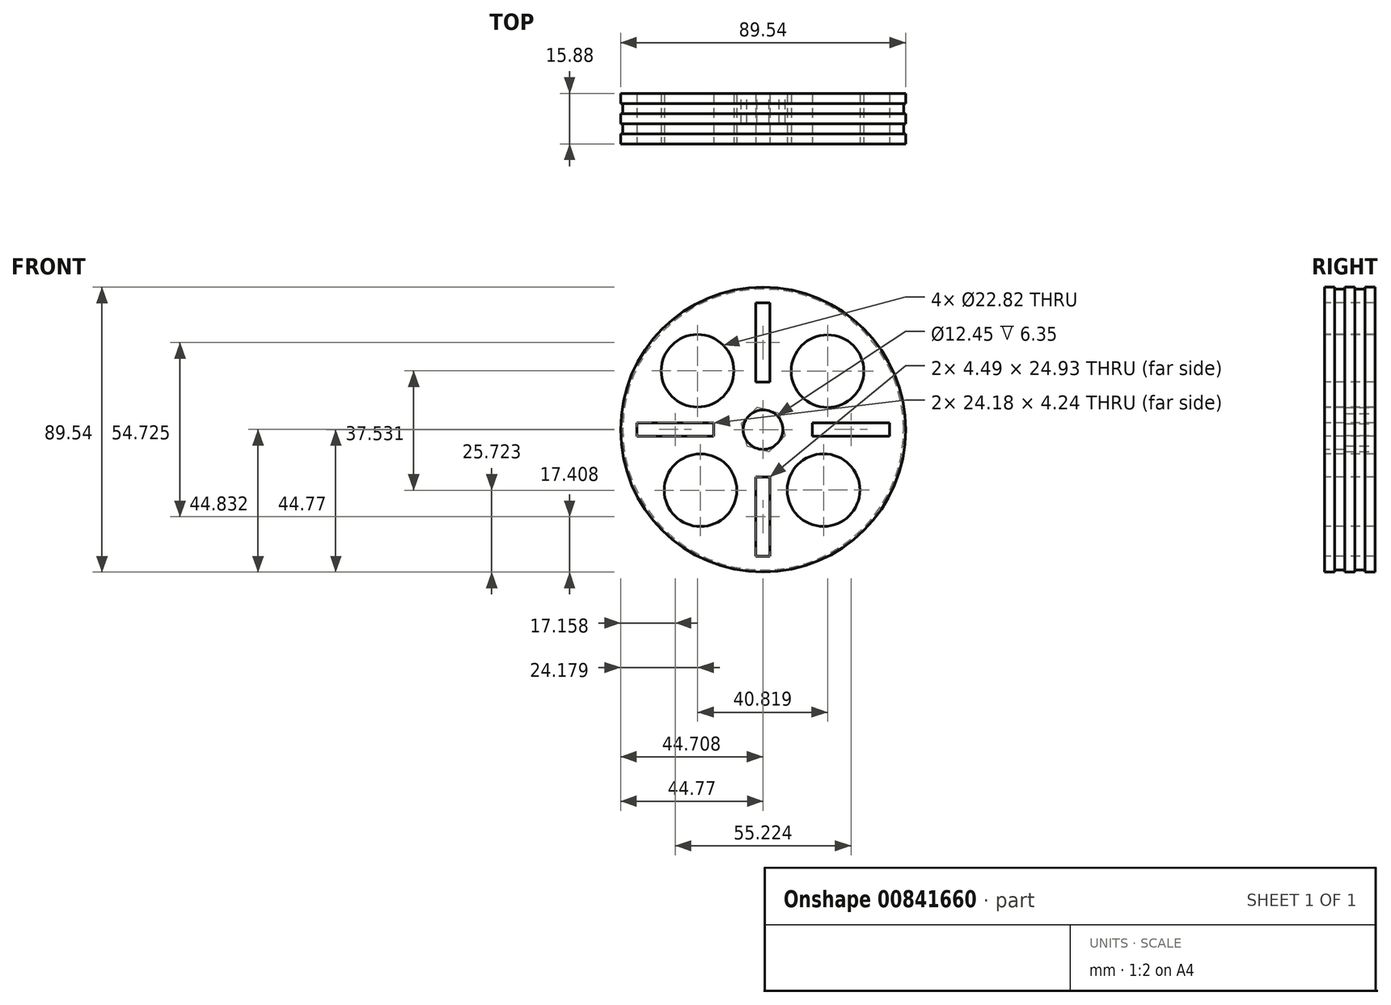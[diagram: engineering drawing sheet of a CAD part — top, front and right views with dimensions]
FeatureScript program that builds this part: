
annotation { "Feature Type Name" : "Feature", "Feature Type Description" : "" }
export const myFeature = defineFeature(function(context is Context, id is Id, definition is map)
    precondition{}
    {
        {
            var Q0;
            Q0=qCreatedBy(makeId("Front.planeOp"),FACE);
            var sketch = newSketch(context, id + "F0", { "sketchPlane" : qUnion([Q0])});
            skCircle(sketch, "E0", {"center": v(0, 0) * mm, "radius": 44.13 * mm});
            skSolve(sketch);
        }
        {
            var Q0;
            Q0 = qSketchRegion(id + "F0", true);
            extrude(context, id + "F1", {"entities" : qUnion([Q0]), "oppositeDirection" : true, "depth" : 3.17 * mm, "offsetDistance" : 25.4 * mm});
        }
        {
            var Q0;
            Q0=qCreatedBy(makeId("Front.planeOp"),FACE);
            var sketch = newSketch(context, id + "F2", { "sketchPlane" : qUnion([Q0])});
            skCircle(sketch, "E1", {"center": v(0, 0) * mm, "radius": 44.77 * mm});
            skSolve(sketch);
        }
        {
            var Q0;
            Q0 = qSketchRegion(id + "F2", true);
            var Q1;
            Q1 = qSketchRegion(id + "F0", true);
            extrude(context, id + "F3", {"entities" : qUnion([Q0, Q1]), "operationType" : NewBodyOperationType.ADD, "depth" : 3.17 * mm, "offsetDistance" : 25.4 * mm});
        }
        {
            var Q0;
            Q0=makeQuery(id+"F3.boolean.opBoolean","MERGE",FACE,{"derivedFrom":[makeQuery(id+"F3.opExtrude","CAP_FACE",FACE,{"disambiguationData":[OSD([sQuery(id+"F0.wireOp",EDGE,"E0")])],"isStart":false}),makeQuery(id+"F3.opExtrude","CAP_FACE",FACE,{"disambiguationData":[OSD([sQuery(id+"F2.wireOp",EDGE,"E1")])],"isStart":false})]});
            var sketch = newSketch(context, id + "F4", { "sketchPlane" : qUnion([Q0])});
            skCircle(sketch, "E2", {"center": v(0, 0) * mm, "radius": 44.13 * mm});
            skSolve(sketch);
        }
        {
            var Q0;
            Q0 = qSketchRegion(id + "F4", true);
            extrude(context, id + "F5", {"entities" : qUnion([Q0]), "operationType" : NewBodyOperationType.ADD, "depth" : 3.17 * mm, "offsetDistance" : 25.4 * mm});
        }
        {
            var Q0;
            Q0=makeQuery(id+"F5.opExtrude","CAP_FACE",FACE,{"disambiguationData":[OSD([sQuery(id+"F4.wireOp",EDGE,"E2")])],"isStart":false});
            var sketch = newSketch(context, id + "F6", { "sketchPlane" : qUnion([Q0])});
            skCircle(sketch, "E3", {"center": v(0, 0) * mm, "radius": 44.77 * mm});
            skSolve(sketch);
        }
        {
            var Q0;
            Q0 = qSketchRegion(id + "F6", true);
            extrude(context, id + "F7", {"entities" : qUnion([Q0]), "operationType" : NewBodyOperationType.ADD, "depth" : 3.17 * mm, "offsetDistance" : 25.4 * mm});
        }
        {
            var Q0;
            Q0=makeQuery(id+"F1.opExtrude","CAP_FACE",FACE,{"disambiguationData":[OSD([sQuery(id+"F0.wireOp",EDGE,"E0")])],"isStart":false});
            var sketch = newSketch(context, id + "F8", { "sketchPlane" : qUnion([Q0])});
            skCircle(sketch, "E4", {"center": v(0, 0) * mm, "radius": 44.77 * mm});
            skSolve(sketch);
        }
        {
            var Q0;
            Q0 = qSketchRegion(id + "F8", true);
            extrude(context, id + "F9", {"entities" : qUnion([Q0]), "operationType" : NewBodyOperationType.ADD, "depth" : 3.17 * mm, "offsetDistance" : 25.4 * mm});
        }
        {
            var Q0;
            Q0=makeQuery(id+"F7.opExtrude","CAP_FACE",FACE,{"disambiguationData":[OSD([sQuery(id+"F6.wireOp",EDGE,"E3")])],"isStart":false});
            var sketch = newSketch(context, id + "F10", { "sketchPlane" : qUnion([Q0])});
            skCircle(sketch, "E5", {"center": v(0, 0) * mm, "radius": 2.03 * mm});
            skSolve(sketch);
        }
        {
            var Q0;
            Q0 = qSketchRegion(id + "F10", true);
            extrude(context, id + "F11", {"entities" : qUnion([Q0]), "operationType" : NewBodyOperationType.REMOVE, "oppositeDirection" : true, "depth" : 152.4 * mm, "offsetDistance" : 25.4 * mm});
        }
        {
            var Q0;
            Q0=makeQuery(id+"F9.opExtrude","CAP_FACE",FACE,{"disambiguationData":[OSD([sQuery(id+"F8.wireOp",EDGE,"E4")])],"isStart":false});
            var sketch = newSketch(context, id + "F12", { "sketchPlane" : qUnion([Q0])});
            skCircle(sketch, "E6.cCircle", {"center": v(0, 0) * mm, "radius": 6.22 * mm, "construction": true});
            skLineSegment(sketch, "E6.0", {"start": v(6.95, 1.84) * mm, "end": v(5.06, -5.1) * mm});
            skLineSegment(sketch, "E6.1", {"start": v(5.06, -5.1) * mm, "end": v(-1.88, -6.93) * mm});
            skLineSegment(sketch, "E6.2", {"start": v(-1.88, -6.93) * mm, "end": v(-6.95, -1.84) * mm});
            skLineSegment(sketch, "E6.3", {"start": v(-6.95, -1.84) * mm, "end": v(-5.06, 5.1) * mm});
            skLineSegment(sketch, "E6.4", {"start": v(-5.06, 5.1) * mm, "end": v(1.88, 6.93) * mm});
            skLineSegment(sketch, "E6.5", {"start": v(1.88, 6.93) * mm, "end": v(6.95, 1.84) * mm});
            skPoint(sketch, "E6.0.midPoint", {"position": v(6, -1.63) * mm});
            skSolve(sketch);
        }
        {
            var Q0;
            Q0 = qSketchRegion(id + "F12", true);
            extrude(context, id + "F13", {"entities" : qUnion([Q0]), "operationType" : NewBodyOperationType.REMOVE, "oppositeDirection" : true, "depth" : 9.52 * mm, "offsetDistance" : 25.4 * mm});
        }
        {
            var Q0;
            Q0=makeQuery(id+"F7.opExtrude","CAP_FACE",FACE,{"disambiguationData":[OSD([sQuery(id+"F6.wireOp",EDGE,"E3")])],"isStart":false});
            var sketch = newSketch(context, id + "F14", { "sketchPlane" : qUnion([Q0])});
            skCircle(sketch, "E7", {"center": v(0, 0) * mm, "radius": 6.22 * mm});
            skSolve(sketch);
        }
        {
            var Q0;
            Q0 = qSketchRegion(id + "F14", true);
            extrude(context, id + "F15", {"entities" : qUnion([Q0]), "operationType" : NewBodyOperationType.REMOVE, "oppositeDirection" : true, "depth" : 14.73 * mm, "offsetDistance" : 25.4 * mm});
        }
        {
            var Q0;
            Q0=makeQuery(id+"F7.opExtrude","CAP_FACE",FACE,{"disambiguationData":[OSD([sQuery(id+"F6.wireOp",EDGE,"E3")])],"isStart":false});
            var sketch = newSketch(context, id + "F16", { "sketchPlane" : qUnion([Q0])});
            skCircle(sketch, "E8", {"center": v(0, 0) * mm, "radius": 15.36 * mm});
            skSolve(sketch);
        }
        {
            var Q0;
            Q0=makeQuery(id+"F16.imprint","IMPRINT",FACE,{"disambiguationData":[TD([[makeQuery(id+"F16.imprint","IMPRINT",EDGE,{"derivedFrom":sQuery(id+"F16.wireOp",EDGE,"E8")}),1.0]])]});
            var sketch = newSketch(context, id + "F17", { "sketchPlane" : qUnion([Q0])});
            skLineSegment(sketch, "E9.bottom", {"start": v(-15.52, -2.06) * mm, "end": v(-39.7, -2.06) * mm});
            skLineSegment(sketch, "E9.top", {"start": v(-15.52, 2.18) * mm, "end": v(-39.7, 2.18) * mm});
            skLineSegment(sketch, "E9.left", {"start": v(-15.52, -2.06) * mm, "end": v(-15.52, 2.18) * mm});
            skLineSegment(sketch, "E9.right", {"start": v(-39.7, -2.06) * mm, "end": v(-39.7, 2.18) * mm});
            skLineSegment(sketch, "E10.bottom", {"start": v(-2.3, 14.9) * mm, "end": v(2.18, 14.9) * mm});
            skLineSegment(sketch, "E10.top", {"start": v(-2.3, 39.83) * mm, "end": v(2.18, 39.83) * mm});
            skLineSegment(sketch, "E10.left", {"start": v(-2.3, 14.9) * mm, "end": v(-2.3, 39.83) * mm});
            skLineSegment(sketch, "E10.right", {"start": v(2.18, 14.9) * mm, "end": v(2.18, 39.83) * mm});
            skLineSegment(sketch, "E11.MirrorCS", {"start": v(15.52, 2.18) * mm, "end": v(39.7, 2.18) * mm});
            skLineSegment(sketch, "E12.MirrorCS", {"start": v(15.52, -2.06) * mm, "end": v(15.52, 2.18) * mm});
            skLineSegment(sketch, "E13.MirrorCS", {"start": v(15.52, -2.06) * mm, "end": v(39.7, -2.06) * mm});
            skLineSegment(sketch, "E14.MirrorCS", {"start": v(39.7, -2.06) * mm, "end": v(39.7, 2.18) * mm});
            skLineSegment(sketch, "E15.MirrorCS", {"start": v(-2.3, -14.9) * mm, "end": v(-2.3, -39.83) * mm});
            skLineSegment(sketch, "E16.MirrorCS", {"start": v(2.18, -14.9) * mm, "end": v(2.18, -39.83) * mm});
            skLineSegment(sketch, "E17.MirrorCS", {"start": v(-2.3, -14.9) * mm, "end": v(2.18, -14.9) * mm});
            skLineSegment(sketch, "E18.MirrorCS", {"start": v(-2.3, -39.83) * mm, "end": v(2.18, -39.83) * mm});
            skSolve(sketch);
        }
        {
            var Q0;
            Q0 = qSketchRegion(id + "F17", true);
            extrude(context, id + "F18", {"entities" : qUnion([Q0]), "operationType" : NewBodyOperationType.REMOVE, "oppositeDirection" : true, "depth" : 25.4 * mm, "offsetDistance" : 25.4 * mm});
        }
        {
            var Q0;
            Q0=makeQuery(id+"F16.imprint","IMPRINT",FACE,{"disambiguationData":[TD([[makeQuery(id+"F16.imprint","IMPRINT",EDGE,{"derivedFrom":sQuery(id+"F16.wireOp",EDGE,"E8")}),-1.0]])]});
            var sketch = newSketch(context, id + "F19", { "sketchPlane" : qUnion([Q0])});
            skCircle(sketch, "E19", {"center": v(-20.6, 18.48) * mm, "radius": 11.4 * mm});
            skCircle(sketch, "E20", {"center": v(-19.67, -19.05) * mm, "radius": 11.4 * mm});
            skCircle(sketch, "E21", {"center": v(18.98, -19.01) * mm, "radius": 11.4 * mm});
            skCircle(sketch, "E22", {"center": v(20.23, 18.39) * mm, "radius": 11.4 * mm});
            skSolve(sketch);
        }
        {
            var Q0;
            Q0 = qSketchRegion(id + "F19", true);
            extrude(context, id + "F20", {"entities" : qUnion([Q0]), "operationType" : NewBodyOperationType.REMOVE, "oppositeDirection" : true, "depth" : 25.4 * mm, "offsetDistance" : 25.4 * mm});
        }
    });
